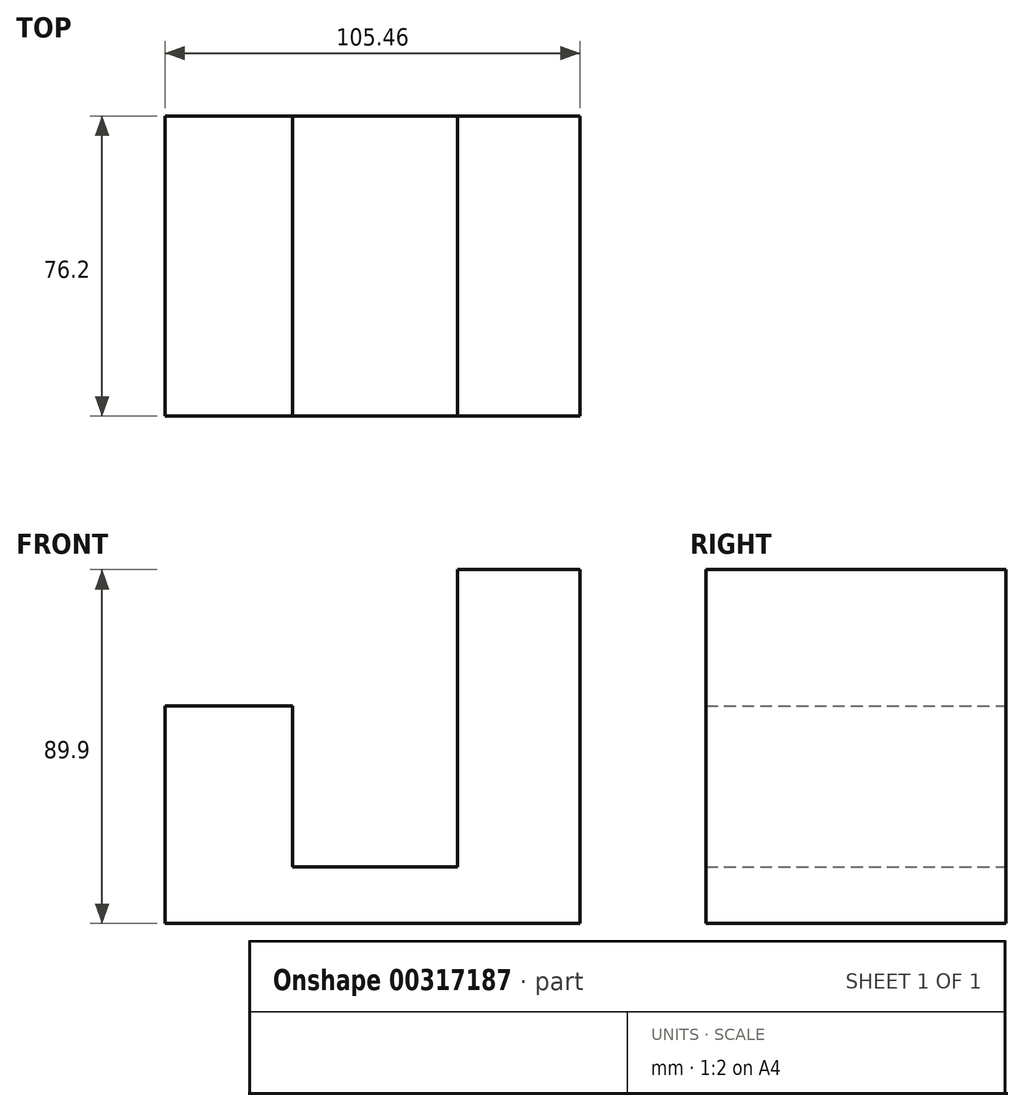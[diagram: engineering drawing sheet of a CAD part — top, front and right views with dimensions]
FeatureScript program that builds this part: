
annotation { "Feature Type Name" : "Feature", "Feature Type Description" : "" }
export const myFeature = defineFeature(function(context is Context, id is Id, definition is map)
    precondition{}
    {
        {
            var Q0;
            Q0=qCreatedBy(makeId("Front.planeOp"),FACE);
            var sketch = newSketch(context, id + "F0", { "sketchPlane" : qUnion([Q0])});
            skLineSegment(sketch, "E0", {"start": v(23.84, 26.55) * mm, "end": v(54.97, 26.55) * mm});
            skLineSegment(sketch, "E1", {"start": v(54.97, 26.55) * mm, "end": v(54.97, -63.35) * mm});
            skLineSegment(sketch, "E2", {"start": v(54.97, -63.35) * mm, "end": v(-50.5, -63.35) * mm});
            skLineSegment(sketch, "E3", {"start": v(-50.5, -63.35) * mm, "end": v(-50.5, -8.08) * mm});
            skLineSegment(sketch, "E4", {"start": v(-50.5, -8.08) * mm, "end": v(-18.1, -8.08) * mm});
            skLineSegment(sketch, "E5", {"start": v(-18.1, -8.08) * mm, "end": v(-18.1, -49.06) * mm});
            skLineSegment(sketch, "E6", {"start": v(-18.1, -49.06) * mm, "end": v(23.84, -49.06) * mm});
            skLineSegment(sketch, "E7", {"start": v(23.84, -49.06) * mm, "end": v(23.84, -43.66) * mm});
            skLineSegment(sketch, "E8", {"start": v(23.84, 26.55) * mm, "end": v(23.84, -49.06) * mm});
            skSolve(sketch);
        }
        {
            var Q0;
            {var subQ0=sQuery(id+"F0.wireOp",EDGE,"E0");Q0=makeQuery(id+"F0.imprint","IMPRINT",FACE,{"disambiguationData":[TD([[makeQuery(id+"F0.imprint","IMPRINT",EDGE,{"derivedFrom":subQ0}),-1.0]])]});}
            extrude(context, id + "F1", {"entities" : qUnion([Q0]), "depth" : 76.2 * mm});
        }
    });
